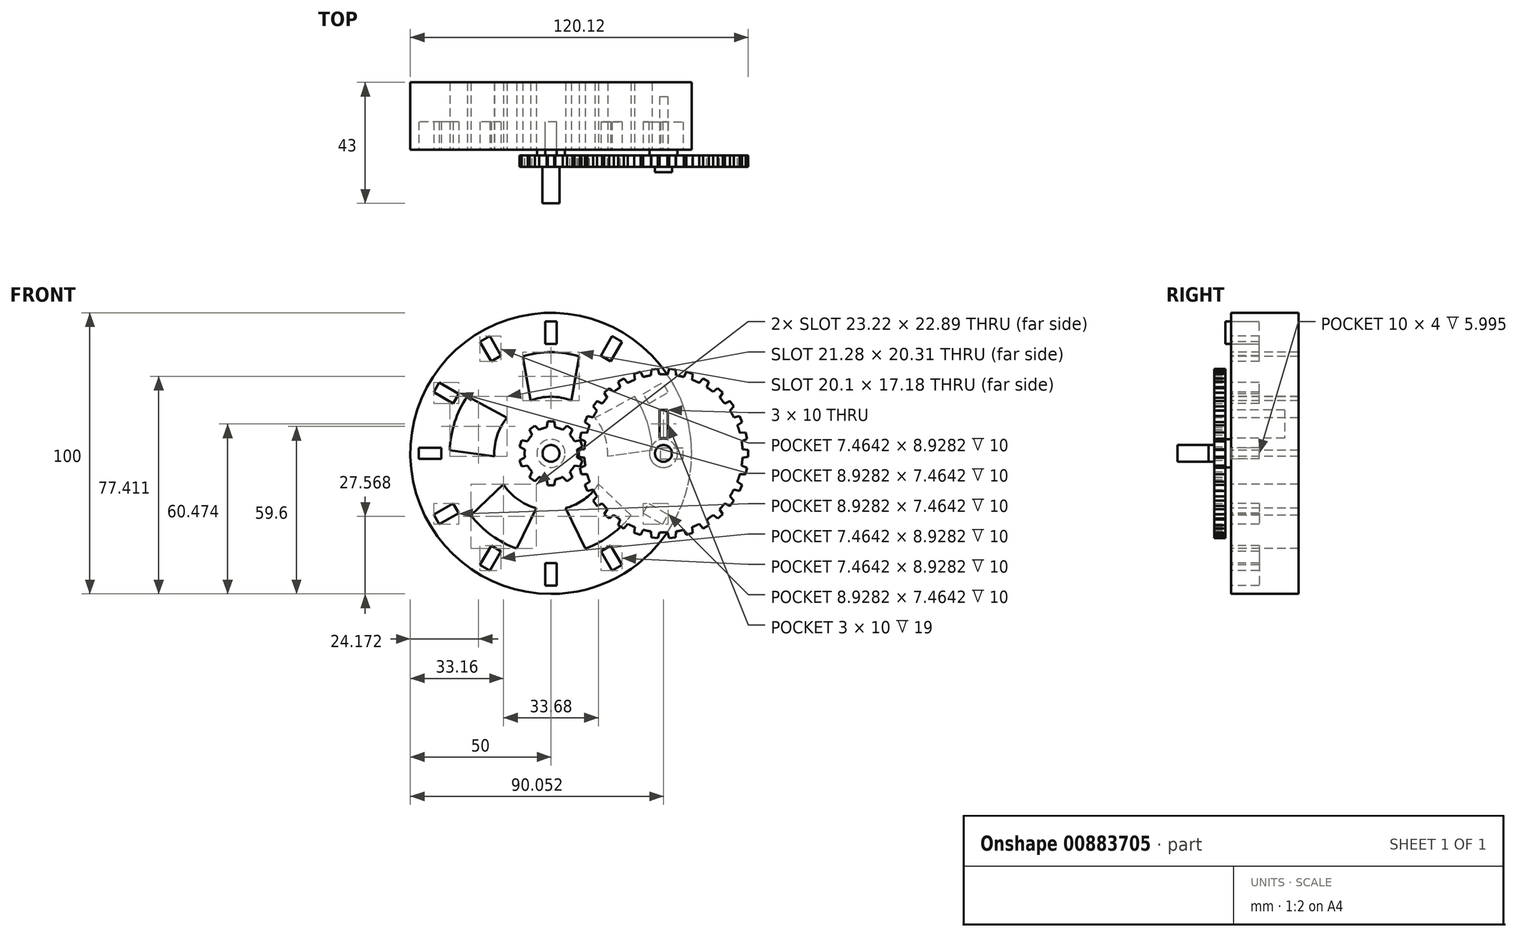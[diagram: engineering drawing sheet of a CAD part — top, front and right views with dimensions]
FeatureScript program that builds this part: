
annotation { "Feature Type Name" : "Feature", "Feature Type Description" : "" }
export const myFeature = defineFeature(function(context is Context, id is Id, definition is map)
    precondition{}
    {
        {
            assignVariable(context, id + "F0", {"name" : "DA", "anyValue" : 40});
        }
        {
            assignVariable(context, id + "F1", {"name" : "M", "anyValue" : 2.5});
        }
        {
            var Q0;
            Q0=qCreatedBy(makeId("Front.planeOp"),FACE);
            var sketch = newSketch(context, id + "F2", { "sketchPlane" : qUnion([Q0])});
            skCircle(sketch, "E0", {"center": v(0, 0) * mm, "radius": 50 * mm});
            skSolve(sketch);
        }
        {
            var Q0;
            Q0 = qSketchRegion(id + "F2", true);
            extrude(context, id + "F3", {"entities" : qUnion([Q0]), "depth" : 24 * mm, "offsetDistance" : 25 * mm});
        }
        {
            var Q0;
            Q0=makeQuery(id+"F3.opExtrude","CAP_FACE",FACE,{"disambiguationData":[OSD([sQuery(id+"F2.wireOp",EDGE,"E0")])],"isStart":false});
            var sketch = newSketch(context, id + "F4", { "sketchPlane" : qUnion([Q0])});
            skCircle(sketch, "E1", {"center": v(0, 0) * mm, "radius": 5 * mm});
            skCircle(sketch, "E2", {"center": v(40, 0) * mm, "radius": 5 * mm});
            skCircle(sketch, "E3", {"center": v(0, 0) * mm, "radius": 3 * mm});
            skCircle(sketch, "E4", {"center": v(40, 0) * mm, "radius": 3 * mm});
            skSolve(sketch);
        }
        {
            var Q0;
            Q0 = qSketchRegion(id + "F4", true);
            extrude(context, id + "F5", {"entities" : qUnion([Q0]), "operationType" : NewBodyOperationType.ADD, "depth" : 2 * mm, "offsetDistance" : 25 * mm});
        }
        {
            var Q0;
            Q0=makeQuery(id+"F5.boolean.opBoolean","SPLIT",FACE,{"disambiguationData":[TD([makeQuery(id+"F5.opExtrude","SWEPT_FACE",FACE,{"disambiguationData":[OSD([sQuery(id+"F4.wireOp",EDGE,"E3")])]})])],"derivedFrom":makeQuery(id+"F3.opExtrude","CAP_FACE",FACE,{"disambiguationData":[OSD([sQuery(id+"F2.wireOp",EDGE,"E0")])],"isStart":false})});
            extrude(context, id + "F6", {"entities" : qUnion([Q0]), "depth" : 19 * mm, "offsetDistance" : 25 * mm});
        }
        {
            var Q0;
            Q0=makeQuery(id+"F5.boolean.opBoolean","SPLIT",FACE,{"disambiguationData":[TD([makeQuery(id+"F5.opExtrude","SWEPT_FACE",FACE,{"disambiguationData":[OSD([sQuery(id+"F4.wireOp",EDGE,"E4")])]})])],"derivedFrom":makeQuery(id+"F3.opExtrude","CAP_FACE",FACE,{"disambiguationData":[OSD([sQuery(id+"F2.wireOp",EDGE,"E0")])],"isStart":false})});
            extrude(context, id + "F7", {"entities" : qUnion([Q0]), "depth" : 8 * mm, "offsetDistance" : 25 * mm});
        }
        {
            assignVariable(context, id + "F8", {"name" : "M", "anyValue" : 2.5});
        }
        {
            assignVariable(context, id + "F9", {"name" : "S", "anyValue" : 0.8});
        }
        {
            assignVariable(context, id + "F10", {"name" : "DL", "anyValue" : (getVariable(context, 'DA') - getVariable(context, 'M')) / 2});
        }
        {
            var Q0;
            Q0=makeQuery(id+"F5.opExtrude","CAP_FACE",FACE,{"disambiguationData":[OSD([sQuery(id+"F4.wireOp",EDGE,"E1"),sQuery(id+"F4.wireOp",EDGE,"E3")])],"isStart":false});
            var sketch = newSketch(context, id + "F11", { "sketchPlane" : qUnion([Q0])});
            skCircle(sketch, "E5", {"center": v(0, 0) * mm, "radius": 9.38 * mm});
            skLineSegment(sketch, "E6", {"start": v(1.55, 9.25) * mm, "end": v(1.18, 11.38) * mm});
            skLineSegment(sketch, "E7", {"start": v(1.18, 11.38) * mm, "end": v(0, 11.38) * mm});
            skLineSegment(sketch, "E8.MirrorCS", {"start": v(-1.18, 11.38) * mm, "end": v(0, 11.38) * mm});
            skLineSegment(sketch, "E9.MirrorCS", {"start": v(-1.55, 9.25) * mm, "end": v(-1.18, 11.38) * mm});
            skLineSegment(sketch, "E10.1.0", {"start": v(-5.73, 9.9) * mm, "end": v(-6.69, 9.2) * mm});
            skLineSegment(sketch, "E10.1.1", {"start": v(-7.64, 8.51) * mm, "end": v(-6.69, 9.2) * mm});
            skLineSegment(sketch, "E10.1.2", {"start": v(-6.7, 6.57) * mm, "end": v(-7.64, 8.51) * mm});
            skLineSegment(sketch, "E10.1.3", {"start": v(-4.18, 8.4) * mm, "end": v(-5.73, 9.9) * mm});
            skLineSegment(sketch, "E10.2.0", {"start": v(-10.45, 4.64) * mm, "end": v(-10.82, 3.52) * mm});
            skLineSegment(sketch, "E10.2.1", {"start": v(-11.18, 2.4) * mm, "end": v(-10.82, 3.52) * mm});
            skLineSegment(sketch, "E10.2.2", {"start": v(-9.27, 1.38) * mm, "end": v(-11.18, 2.4) * mm});
            skLineSegment(sketch, "E10.2.3", {"start": v(-8.31, 4.33) * mm, "end": v(-10.45, 4.64) * mm});
            skLineSegment(sketch, "E11.2.3.0", {"start": v(-11.18, -2.4) * mm, "end": v(-10.82, -3.52) * mm});
            skLineSegment(sketch, "E11.3.3.0", {"start": v(-10.45, -4.64) * mm, "end": v(-10.82, -3.52) * mm});
            skLineSegment(sketch, "E11.6.3.0", {"start": v(-8.31, -4.33) * mm, "end": v(-10.45, -4.64) * mm});
            skLineSegment(sketch, "E11.9.3.0", {"start": v(-9.27, -1.38) * mm, "end": v(-11.18, -2.4) * mm});
            skLineSegment(sketch, "E11.2.4.0", {"start": v(-7.64, -8.51) * mm, "end": v(-6.69, -9.2) * mm});
            skLineSegment(sketch, "E11.3.4.0", {"start": v(-5.73, -9.9) * mm, "end": v(-6.69, -9.2) * mm});
            skLineSegment(sketch, "E11.6.4.0", {"start": v(-4.18, -8.4) * mm, "end": v(-5.73, -9.9) * mm});
            skLineSegment(sketch, "E11.9.4.0", {"start": v(-6.7, -6.57) * mm, "end": v(-7.64, -8.51) * mm});
            skLineSegment(sketch, "E11.2.5.0", {"start": v(-1.18, -11.38) * mm, "end": v(0, -11.38) * mm});
            skLineSegment(sketch, "E11.3.5.0", {"start": v(1.18, -11.38) * mm, "end": v(0, -11.38) * mm});
            skLineSegment(sketch, "E11.6.5.0", {"start": v(1.55, -9.25) * mm, "end": v(1.18, -11.38) * mm});
            skLineSegment(sketch, "E11.9.5.0", {"start": v(-1.55, -9.25) * mm, "end": v(-1.18, -11.38) * mm});
            skLineSegment(sketch, "E11.2.6.0", {"start": v(5.73, -9.9) * mm, "end": v(6.69, -9.2) * mm});
            skLineSegment(sketch, "E11.3.6.0", {"start": v(7.64, -8.51) * mm, "end": v(6.69, -9.2) * mm});
            skLineSegment(sketch, "E11.6.6.0", {"start": v(6.7, -6.57) * mm, "end": v(7.64, -8.51) * mm});
            skLineSegment(sketch, "E11.9.6.0", {"start": v(4.18, -8.4) * mm, "end": v(5.73, -9.9) * mm});
            skLineSegment(sketch, "E11.2.7.0", {"start": v(10.45, -4.64) * mm, "end": v(10.82, -3.52) * mm});
            skLineSegment(sketch, "E11.3.7.0", {"start": v(11.18, -2.4) * mm, "end": v(10.82, -3.52) * mm});
            skLineSegment(sketch, "E11.6.7.0", {"start": v(9.27, -1.38) * mm, "end": v(11.18, -2.4) * mm});
            skLineSegment(sketch, "E11.9.7.0", {"start": v(8.31, -4.33) * mm, "end": v(10.45, -4.64) * mm});
            skLineSegment(sketch, "E11.2.8.0", {"start": v(11.18, 2.4) * mm, "end": v(10.82, 3.52) * mm});
            skLineSegment(sketch, "E11.3.8.0", {"start": v(10.45, 4.64) * mm, "end": v(10.82, 3.52) * mm});
            skLineSegment(sketch, "E11.6.8.0", {"start": v(8.31, 4.33) * mm, "end": v(10.45, 4.64) * mm});
            skLineSegment(sketch, "E11.9.8.0", {"start": v(9.27, 1.38) * mm, "end": v(11.18, 2.4) * mm});
            skLineSegment(sketch, "E11.2.9.0", {"start": v(7.64, 8.51) * mm, "end": v(6.69, 9.2) * mm});
            skLineSegment(sketch, "E11.3.9.0", {"start": v(5.73, 9.9) * mm, "end": v(6.69, 9.2) * mm});
            skLineSegment(sketch, "E11.6.9.0", {"start": v(4.18, 8.4) * mm, "end": v(5.73, 9.9) * mm});
            skLineSegment(sketch, "E11.9.9.0", {"start": v(6.7, 6.57) * mm, "end": v(7.64, 8.51) * mm});
            skSolve(sketch);
        }
        {
            var Q0;
            Q0 = qSketchRegion(id + "F11", true);
            extrude(context, id + "F12", {"entities" : qUnion([Q0]), "operationType" : NewBodyOperationType.ADD, "depth" : 4 * mm, "offsetDistance" : 25 * mm});
        }
        {
            var Q0;
            Q0=makeQuery(id+"F5.opExtrude","CAP_FACE",FACE,{"disambiguationData":[OSD([sQuery(id+"F4.wireOp",EDGE,"E2"),sQuery(id+"F4.wireOp",EDGE,"E4")])],"isStart":false});
            var sketch = newSketch(context, id + "F13", { "sketchPlane" : qUnion([Q0])});
            skCircle(sketch, "E12", {"center": v(40, 0) * mm, "radius": 28.12 * mm});
            skLineSegment(sketch, "E13", {"start": v(11.92, 1.54) * mm, "end": v(9.88, 1.18) * mm});
            skLineSegment(sketch, "E14", {"start": v(9.88, 1.18) * mm, "end": v(9.88, 0) * mm});
            skLineSegment(sketch, "E15.MirrorCS", {"start": v(9.88, -1.18) * mm, "end": v(9.88, 0) * mm});
            skLineSegment(sketch, "E16.MirrorCS", {"start": v(11.92, -1.54) * mm, "end": v(9.88, -1.18) * mm});
            skLineSegment(sketch, "E17.1.0", {"start": v(12.21, -4.33) * mm, "end": v(10.29, -5.11) * mm});
            skLineSegment(sketch, "E17.1.1", {"start": v(10.29, -5.11) * mm, "end": v(10.53, -6.26) * mm});
            skLineSegment(sketch, "E17.1.2", {"start": v(10.78, -7.42) * mm, "end": v(10.53, -6.26) * mm});
            skLineSegment(sketch, "E17.1.3", {"start": v(12.85, -7.34) * mm, "end": v(10.78, -7.42) * mm});
            skLineSegment(sketch, "E17.2.0", {"start": v(13.72, -10.02) * mm, "end": v(12, -11.18) * mm});
            skLineSegment(sketch, "E17.2.1", {"start": v(12, -11.18) * mm, "end": v(12.48, -12.25) * mm});
            skLineSegment(sketch, "E17.2.2", {"start": v(12.96, -13.33) * mm, "end": v(12.48, -12.25) * mm});
            skLineSegment(sketch, "E17.2.3", {"start": v(14.97, -12.83) * mm, "end": v(12.96, -13.33) * mm});
            skLineSegment(sketch, "E18.2.3.0", {"start": v(16.38, -15.26) * mm, "end": v(14.94, -16.75) * mm});
            skLineSegment(sketch, "E18.3.3.0", {"start": v(14.94, -16.75) * mm, "end": v(15.63, -17.7) * mm});
            skLineSegment(sketch, "E18.6.3.0", {"start": v(16.32, -18.66) * mm, "end": v(15.63, -17.7) * mm});
            skLineSegment(sketch, "E18.9.3.0", {"start": v(18.18, -17.75) * mm, "end": v(16.32, -18.66) * mm});
            skLineSegment(sketch, "E18.2.4.0", {"start": v(20.07, -19.84) * mm, "end": v(18.97, -21.6) * mm});
            skLineSegment(sketch, "E18.3.4.0", {"start": v(18.97, -21.6) * mm, "end": v(19.84, -22.39) * mm});
            skLineSegment(sketch, "E18.6.4.0", {"start": v(20.72, -23.18) * mm, "end": v(19.84, -22.39) * mm});
            skLineSegment(sketch, "E18.9.4.0", {"start": v(22.35, -21.9) * mm, "end": v(20.72, -23.18) * mm});
            skLineSegment(sketch, "E18.2.5.0", {"start": v(24.63, -23.55) * mm, "end": v(23.92, -25.5) * mm});
            skLineSegment(sketch, "E18.3.5.0", {"start": v(23.92, -25.5) * mm, "end": v(24.94, -26.09) * mm});
            skLineSegment(sketch, "E18.6.5.0", {"start": v(25.96, -26.68) * mm, "end": v(24.94, -26.09) * mm});
            skLineSegment(sketch, "E18.9.5.0", {"start": v(27.3, -25.09) * mm, "end": v(25.96, -26.68) * mm});
            skLineSegment(sketch, "E18.2.6.0", {"start": v(29.86, -26.23) * mm, "end": v(29.57, -28.29) * mm});
            skLineSegment(sketch, "E18.3.6.0", {"start": v(29.57, -28.29) * mm, "end": v(30.7, -28.65) * mm});
            skLineSegment(sketch, "E18.6.6.0", {"start": v(31.81, -29.01) * mm, "end": v(30.7, -28.65) * mm});
            skLineSegment(sketch, "E18.9.6.0", {"start": v(32.78, -27.18) * mm, "end": v(31.81, -29.01) * mm});
            skLineSegment(sketch, "E18.2.7.0", {"start": v(35.53, -27.77) * mm, "end": v(35.68, -29.84) * mm});
            skLineSegment(sketch, "E18.3.7.0", {"start": v(35.68, -29.84) * mm, "end": v(36.85, -29.96) * mm});
            skLineSegment(sketch, "E18.6.7.0", {"start": v(38.02, -30.08) * mm, "end": v(36.85, -29.96) * mm});
            skLineSegment(sketch, "E18.9.7.0", {"start": v(38.6, -28.09) * mm, "end": v(38.02, -30.08) * mm});
            skLineSegment(sketch, "E18.2.8.0", {"start": v(41.4, -28.09) * mm, "end": v(41.98, -30.08) * mm});
            skLineSegment(sketch, "E18.3.8.0", {"start": v(41.98, -30.08) * mm, "end": v(43.15, -29.96) * mm});
            skLineSegment(sketch, "E18.6.8.0", {"start": v(44.32, -29.84) * mm, "end": v(43.15, -29.96) * mm});
            skLineSegment(sketch, "E18.9.8.0", {"start": v(44.47, -27.77) * mm, "end": v(44.32, -29.84) * mm});
            skLineSegment(sketch, "E18.2.9.0", {"start": v(47.22, -27.18) * mm, "end": v(48.19, -29.01) * mm});
            skLineSegment(sketch, "E18.3.9.0", {"start": v(48.19, -29.01) * mm, "end": v(49.3, -28.65) * mm});
            skLineSegment(sketch, "E18.6.9.0", {"start": v(50.43, -28.29) * mm, "end": v(49.3, -28.65) * mm});
            skLineSegment(sketch, "E18.9.9.0", {"start": v(50.14, -26.23) * mm, "end": v(50.43, -28.29) * mm});
            skLineSegment(sketch, "E18.2.10.0", {"start": v(52.7, -25.09) * mm, "end": v(54.04, -26.68) * mm});
            skLineSegment(sketch, "E18.3.10.0", {"start": v(54.04, -26.68) * mm, "end": v(55.06, -26.09) * mm});
            skLineSegment(sketch, "E18.6.10.0", {"start": v(56.08, -25.5) * mm, "end": v(55.06, -26.09) * mm});
            skLineSegment(sketch, "E18.9.10.0", {"start": v(55.37, -23.55) * mm, "end": v(56.08, -25.5) * mm});
            skLineSegment(sketch, "E18.2.11.0", {"start": v(57.65, -21.9) * mm, "end": v(59.28, -23.18) * mm});
            skLineSegment(sketch, "E18.3.11.0", {"start": v(59.28, -23.18) * mm, "end": v(60.16, -22.39) * mm});
            skLineSegment(sketch, "E18.6.11.0", {"start": v(61.03, -21.6) * mm, "end": v(60.16, -22.39) * mm});
            skLineSegment(sketch, "E18.9.11.0", {"start": v(59.93, -19.84) * mm, "end": v(61.03, -21.6) * mm});
            skLineSegment(sketch, "E18.2.12.0", {"start": v(61.82, -17.75) * mm, "end": v(63.68, -18.66) * mm});
            skLineSegment(sketch, "E18.3.12.0", {"start": v(63.68, -18.66) * mm, "end": v(64.37, -17.7) * mm});
            skLineSegment(sketch, "E18.6.12.0", {"start": v(65.06, -16.75) * mm, "end": v(64.37, -17.7) * mm});
            skLineSegment(sketch, "E18.9.12.0", {"start": v(63.62, -15.26) * mm, "end": v(65.06, -16.75) * mm});
            skLineSegment(sketch, "E18.2.13.0", {"start": v(65.03, -12.83) * mm, "end": v(67.04, -13.33) * mm});
            skLineSegment(sketch, "E18.3.13.0", {"start": v(67.04, -13.33) * mm, "end": v(67.52, -12.25) * mm});
            skLineSegment(sketch, "E18.6.13.0", {"start": v(68, -11.18) * mm, "end": v(67.52, -12.25) * mm});
            skLineSegment(sketch, "E18.9.13.0", {"start": v(66.28, -10.02) * mm, "end": v(68, -11.18) * mm});
            skLineSegment(sketch, "E18.2.14.0", {"start": v(67.15, -7.34) * mm, "end": v(69.22, -7.42) * mm});
            skLineSegment(sketch, "E18.3.14.0", {"start": v(69.22, -7.42) * mm, "end": v(69.47, -6.26) * mm});
            skLineSegment(sketch, "E18.6.14.0", {"start": v(69.71, -5.11) * mm, "end": v(69.47, -6.26) * mm});
            skLineSegment(sketch, "E18.9.14.0", {"start": v(67.79, -4.33) * mm, "end": v(69.71, -5.11) * mm});
            skLineSegment(sketch, "E18.2.15.0", {"start": v(68.08, -1.54) * mm, "end": v(70.13, -1.18) * mm});
            skLineSegment(sketch, "E18.3.15.0", {"start": v(70.12, -1.18) * mm, "end": v(70.12, 0) * mm});
            skLineSegment(sketch, "E18.6.15.0", {"start": v(70.12, 1.18) * mm, "end": v(70.12, 0) * mm});
            skLineSegment(sketch, "E18.9.15.0", {"start": v(68.08, 1.54) * mm, "end": v(70.13, 1.18) * mm});
            skLineSegment(sketch, "E18.2.16.0", {"start": v(67.79, 4.33) * mm, "end": v(69.71, 5.11) * mm});
            skLineSegment(sketch, "E18.3.16.0", {"start": v(69.71, 5.11) * mm, "end": v(69.47, 6.26) * mm});
            skLineSegment(sketch, "E18.6.16.0", {"start": v(69.22, 7.42) * mm, "end": v(69.47, 6.26) * mm});
            skLineSegment(sketch, "E18.9.16.0", {"start": v(67.15, 7.34) * mm, "end": v(69.22, 7.42) * mm});
            skLineSegment(sketch, "E18.2.17.0", {"start": v(66.28, 10.02) * mm, "end": v(68, 11.18) * mm});
            skLineSegment(sketch, "E18.3.17.0", {"start": v(68, 11.18) * mm, "end": v(67.52, 12.25) * mm});
            skLineSegment(sketch, "E18.6.17.0", {"start": v(67.04, 13.33) * mm, "end": v(67.52, 12.25) * mm});
            skLineSegment(sketch, "E18.9.17.0", {"start": v(65.03, 12.83) * mm, "end": v(67.04, 13.33) * mm});
            skLineSegment(sketch, "E18.2.18.0", {"start": v(63.62, 15.26) * mm, "end": v(65.06, 16.75) * mm});
            skLineSegment(sketch, "E18.3.18.0", {"start": v(65.06, 16.75) * mm, "end": v(64.37, 17.7) * mm});
            skLineSegment(sketch, "E18.6.18.0", {"start": v(63.68, 18.66) * mm, "end": v(64.37, 17.7) * mm});
            skLineSegment(sketch, "E18.9.18.0", {"start": v(61.82, 17.75) * mm, "end": v(63.68, 18.66) * mm});
            skLineSegment(sketch, "E18.2.19.0", {"start": v(59.93, 19.84) * mm, "end": v(61.03, 21.6) * mm});
            skLineSegment(sketch, "E18.3.19.0", {"start": v(61.03, 21.6) * mm, "end": v(60.16, 22.39) * mm});
            skLineSegment(sketch, "E18.6.19.0", {"start": v(59.28, 23.18) * mm, "end": v(60.16, 22.39) * mm});
            skLineSegment(sketch, "E18.9.19.0", {"start": v(57.65, 21.9) * mm, "end": v(59.28, 23.18) * mm});
            skLineSegment(sketch, "E18.2.20.0", {"start": v(55.37, 23.55) * mm, "end": v(56.08, 25.5) * mm});
            skLineSegment(sketch, "E18.3.20.0", {"start": v(56.08, 25.5) * mm, "end": v(55.06, 26.09) * mm});
            skLineSegment(sketch, "E18.6.20.0", {"start": v(54.04, 26.68) * mm, "end": v(55.06, 26.09) * mm});
            skLineSegment(sketch, "E18.9.20.0", {"start": v(52.7, 25.09) * mm, "end": v(54.04, 26.68) * mm});
            skLineSegment(sketch, "E18.2.21.0", {"start": v(50.14, 26.23) * mm, "end": v(50.43, 28.29) * mm});
            skLineSegment(sketch, "E18.3.21.0", {"start": v(50.43, 28.29) * mm, "end": v(49.3, 28.65) * mm});
            skLineSegment(sketch, "E18.6.21.0", {"start": v(48.19, 29.01) * mm, "end": v(49.3, 28.65) * mm});
            skLineSegment(sketch, "E18.9.21.0", {"start": v(47.22, 27.18) * mm, "end": v(48.19, 29.01) * mm});
            skLineSegment(sketch, "E18.2.22.0", {"start": v(44.47, 27.77) * mm, "end": v(44.32, 29.84) * mm});
            skLineSegment(sketch, "E18.3.22.0", {"start": v(44.32, 29.84) * mm, "end": v(43.15, 29.96) * mm});
            skLineSegment(sketch, "E18.6.22.0", {"start": v(41.98, 30.08) * mm, "end": v(43.15, 29.96) * mm});
            skLineSegment(sketch, "E18.9.22.0", {"start": v(41.4, 28.09) * mm, "end": v(41.98, 30.08) * mm});
            skLineSegment(sketch, "E18.2.23.0", {"start": v(38.6, 28.09) * mm, "end": v(38.02, 30.08) * mm});
            skLineSegment(sketch, "E18.3.23.0", {"start": v(38.02, 30.08) * mm, "end": v(36.85, 29.96) * mm});
            skLineSegment(sketch, "E18.6.23.0", {"start": v(35.68, 29.84) * mm, "end": v(36.85, 29.96) * mm});
            skLineSegment(sketch, "E18.9.23.0", {"start": v(35.53, 27.77) * mm, "end": v(35.68, 29.84) * mm});
            skLineSegment(sketch, "E18.2.24.0", {"start": v(32.78, 27.18) * mm, "end": v(31.81, 29.01) * mm});
            skLineSegment(sketch, "E18.3.24.0", {"start": v(31.81, 29.01) * mm, "end": v(30.7, 28.65) * mm});
            skLineSegment(sketch, "E18.6.24.0", {"start": v(29.57, 28.29) * mm, "end": v(30.7, 28.65) * mm});
            skLineSegment(sketch, "E18.9.24.0", {"start": v(29.86, 26.23) * mm, "end": v(29.57, 28.29) * mm});
            skLineSegment(sketch, "E18.2.25.0", {"start": v(27.3, 25.09) * mm, "end": v(25.96, 26.68) * mm});
            skLineSegment(sketch, "E18.3.25.0", {"start": v(25.96, 26.68) * mm, "end": v(24.94, 26.09) * mm});
            skLineSegment(sketch, "E18.6.25.0", {"start": v(23.92, 25.5) * mm, "end": v(24.94, 26.09) * mm});
            skLineSegment(sketch, "E18.9.25.0", {"start": v(24.63, 23.55) * mm, "end": v(23.92, 25.5) * mm});
            skLineSegment(sketch, "E18.2.26.0", {"start": v(22.35, 21.9) * mm, "end": v(20.72, 23.18) * mm});
            skLineSegment(sketch, "E18.3.26.0", {"start": v(20.72, 23.18) * mm, "end": v(19.84, 22.39) * mm});
            skLineSegment(sketch, "E18.6.26.0", {"start": v(18.97, 21.6) * mm, "end": v(19.84, 22.39) * mm});
            skLineSegment(sketch, "E18.9.26.0", {"start": v(20.07, 19.84) * mm, "end": v(18.97, 21.6) * mm});
            skLineSegment(sketch, "E18.2.27.0", {"start": v(18.18, 17.75) * mm, "end": v(16.32, 18.66) * mm});
            skLineSegment(sketch, "E18.3.27.0", {"start": v(16.32, 18.66) * mm, "end": v(15.63, 17.7) * mm});
            skLineSegment(sketch, "E18.6.27.0", {"start": v(14.94, 16.75) * mm, "end": v(15.63, 17.7) * mm});
            skLineSegment(sketch, "E18.9.27.0", {"start": v(16.38, 15.26) * mm, "end": v(14.94, 16.75) * mm});
            skLineSegment(sketch, "E18.2.28.0", {"start": v(14.97, 12.83) * mm, "end": v(12.96, 13.33) * mm});
            skLineSegment(sketch, "E18.3.28.0", {"start": v(12.96, 13.33) * mm, "end": v(12.48, 12.25) * mm});
            skLineSegment(sketch, "E18.6.28.0", {"start": v(12, 11.18) * mm, "end": v(12.48, 12.25) * mm});
            skLineSegment(sketch, "E18.9.28.0", {"start": v(13.72, 10.02) * mm, "end": v(12, 11.18) * mm});
            skLineSegment(sketch, "E18.2.29.0", {"start": v(12.85, 7.34) * mm, "end": v(10.78, 7.42) * mm});
            skLineSegment(sketch, "E18.3.29.0", {"start": v(10.78, 7.42) * mm, "end": v(10.53, 6.26) * mm});
            skLineSegment(sketch, "E18.6.29.0", {"start": v(10.29, 5.11) * mm, "end": v(10.53, 6.26) * mm});
            skLineSegment(sketch, "E18.9.29.0", {"start": v(12.21, 4.33) * mm, "end": v(10.29, 5.11) * mm});
            skSolve(sketch);
        }
        {
            var Q0;
            Q0 = qSketchRegion(id + "F13", true);
            extrude(context, id + "F14", {"entities" : qUnion([Q0]), "operationType" : NewBodyOperationType.ADD, "depth" : 4 * mm, "offsetDistance" : 25 * mm});
        }
        {
            var Q0;
            {var subQ0=sQuery(id+"F2.wireOp",EDGE,"E0");Q0=makeQuery(id+"F5.boolean.opBoolean","SPLIT",FACE,{"disambiguationData":[TD([makeQuery(id+"F3.opExtrude","SWEPT_FACE",FACE,{"disambiguationData":[OSD([subQ0])]})])],"derivedFrom":makeQuery(id+"F3.opExtrude","CAP_FACE",FACE,{"disambiguationData":[OSD([subQ0])],"isStart":false})});}
            var sketch = newSketch(context, id + "F15", { "sketchPlane" : qUnion([Q0])});
            skLineSegment(sketch, "E19.bottom", {"start": v(2, 39) * mm, "end": v(-2, 39) * mm});
            skLineSegment(sketch, "E19.top", {"start": v(2, 47) * mm, "end": v(-2, 47) * mm});
            skLineSegment(sketch, "E19.left", {"start": v(2, 39) * mm, "end": v(2, 47) * mm});
            skLineSegment(sketch, "E19.right", {"start": v(-2, 39) * mm, "end": v(-2, 47) * mm});
            skPoint(sketch, "E19.middle", {"position": v(0, 43) * mm});
            skLineSegment(sketch, "E20.1.0", {"start": v(-21.77, 41.7) * mm, "end": v(-25.23, 39.7) * mm});
            skLineSegment(sketch, "E20.1.1", {"start": v(-17.77, 34.77) * mm, "end": v(-21.77, 41.7) * mm});
            skLineSegment(sketch, "E20.1.2", {"start": v(-17.77, 34.77) * mm, "end": v(-21.23, 32.77) * mm});
            skLineSegment(sketch, "E20.1.3", {"start": v(-21.23, 32.77) * mm, "end": v(-25.23, 39.7) * mm});
            skLineSegment(sketch, "E20.2.0", {"start": v(-39.7, 25.23) * mm, "end": v(-41.7, 21.77) * mm});
            skLineSegment(sketch, "E20.2.1", {"start": v(-32.77, 21.23) * mm, "end": v(-39.7, 25.23) * mm});
            skLineSegment(sketch, "E20.2.2", {"start": v(-32.77, 21.23) * mm, "end": v(-34.77, 17.77) * mm});
            skLineSegment(sketch, "E20.2.3", {"start": v(-34.77, 17.77) * mm, "end": v(-41.7, 21.77) * mm});
            skPoint(sketch, "E20.center", {"position": v(0, 0) * mm});
            skLineSegment(sketch, "E21.2.3.0", {"start": v(-47, 2) * mm, "end": v(-47, -2) * mm});
            skLineSegment(sketch, "E21.3.3.0", {"start": v(-39, 2) * mm, "end": v(-47, 2) * mm});
            skLineSegment(sketch, "E21.6.3.0", {"start": v(-39, 2) * mm, "end": v(-39, -2) * mm});
            skLineSegment(sketch, "E21.9.3.0", {"start": v(-39, -2) * mm, "end": v(-47, -2) * mm});
            skLineSegment(sketch, "E21.2.4.0", {"start": v(-41.7, -21.77) * mm, "end": v(-39.7, -25.23) * mm});
            skLineSegment(sketch, "E21.3.4.0", {"start": v(-34.77, -17.77) * mm, "end": v(-41.7, -21.77) * mm});
            skLineSegment(sketch, "E21.6.4.0", {"start": v(-34.77, -17.77) * mm, "end": v(-32.77, -21.23) * mm});
            skLineSegment(sketch, "E21.9.4.0", {"start": v(-32.77, -21.23) * mm, "end": v(-39.7, -25.23) * mm});
            skLineSegment(sketch, "E21.2.5.0", {"start": v(-25.23, -39.7) * mm, "end": v(-21.77, -41.7) * mm});
            skLineSegment(sketch, "E21.3.5.0", {"start": v(-21.23, -32.77) * mm, "end": v(-25.23, -39.7) * mm});
            skLineSegment(sketch, "E21.6.5.0", {"start": v(-21.23, -32.77) * mm, "end": v(-17.77, -34.77) * mm});
            skLineSegment(sketch, "E21.9.5.0", {"start": v(-17.77, -34.77) * mm, "end": v(-21.77, -41.7) * mm});
            skLineSegment(sketch, "E21.2.6.0", {"start": v(-2, -47) * mm, "end": v(2, -47) * mm});
            skLineSegment(sketch, "E21.3.6.0", {"start": v(-2, -39) * mm, "end": v(-2, -47) * mm});
            skLineSegment(sketch, "E21.6.6.0", {"start": v(-2, -39) * mm, "end": v(2, -39) * mm});
            skLineSegment(sketch, "E21.9.6.0", {"start": v(2, -39) * mm, "end": v(2, -47) * mm});
            skLineSegment(sketch, "E21.2.7.0", {"start": v(21.77, -41.7) * mm, "end": v(25.23, -39.7) * mm});
            skLineSegment(sketch, "E21.3.7.0", {"start": v(17.77, -34.77) * mm, "end": v(21.77, -41.7) * mm});
            skLineSegment(sketch, "E21.6.7.0", {"start": v(17.77, -34.77) * mm, "end": v(21.23, -32.77) * mm});
            skLineSegment(sketch, "E21.9.7.0", {"start": v(21.23, -32.77) * mm, "end": v(25.23, -39.7) * mm});
            skLineSegment(sketch, "E21.2.8.0", {"start": v(39.7, -25.23) * mm, "end": v(41.7, -21.77) * mm});
            skLineSegment(sketch, "E21.3.8.0", {"start": v(32.77, -21.23) * mm, "end": v(39.7, -25.23) * mm});
            skLineSegment(sketch, "E21.6.8.0", {"start": v(32.77, -21.23) * mm, "end": v(34.77, -17.77) * mm});
            skLineSegment(sketch, "E21.9.8.0", {"start": v(34.77, -17.77) * mm, "end": v(41.7, -21.77) * mm});
            skLineSegment(sketch, "E21.2.9.0", {"start": v(47, -2) * mm, "end": v(47, 2) * mm});
            skLineSegment(sketch, "E21.3.9.0", {"start": v(39, -2) * mm, "end": v(47, -2) * mm});
            skLineSegment(sketch, "E21.6.9.0", {"start": v(39, -2) * mm, "end": v(39, 2) * mm});
            skLineSegment(sketch, "E21.9.9.0", {"start": v(39, 2) * mm, "end": v(47, 2) * mm});
            skLineSegment(sketch, "E21.2.10.0", {"start": v(41.7, 21.77) * mm, "end": v(39.7, 25.23) * mm});
            skLineSegment(sketch, "E21.3.10.0", {"start": v(34.77, 17.77) * mm, "end": v(41.7, 21.77) * mm});
            skLineSegment(sketch, "E21.6.10.0", {"start": v(34.77, 17.77) * mm, "end": v(32.77, 21.23) * mm});
            skLineSegment(sketch, "E21.9.10.0", {"start": v(32.77, 21.23) * mm, "end": v(39.7, 25.23) * mm});
            skLineSegment(sketch, "E21.2.11.0", {"start": v(25.23, 39.7) * mm, "end": v(21.77, 41.7) * mm});
            skLineSegment(sketch, "E21.3.11.0", {"start": v(21.23, 32.77) * mm, "end": v(25.23, 39.7) * mm});
            skLineSegment(sketch, "E21.6.11.0", {"start": v(21.23, 32.77) * mm, "end": v(17.77, 34.77) * mm});
            skLineSegment(sketch, "E21.9.11.0", {"start": v(17.77, 34.77) * mm, "end": v(21.77, 41.7) * mm});
            skSolve(sketch);
        }
        {
            var Q0;
            Q0 = qSketchRegion(id + "F15", true);
            extrude(context, id + "F16", {"entities" : qUnion([Q0]), "operationType" : NewBodyOperationType.REMOVE, "oppositeDirection" : true, "depth" : 10 * mm, "offsetDistance" : 25 * mm});
        }
        {
            var Q0;
            Q0=makeQuery(id+"F16.boolean.opBoolean","COPY",FACE,{"derivedFrom":makeQuery(id+"F16.opExtrude","CAP_FACE",FACE,{"disambiguationData":[OSD([sQuery(id+"F15.wireOp",EDGE,"E19.bottom"),sQuery(id+"F15.wireOp",EDGE,"E19.top"),sQuery(id+"F15.wireOp",EDGE,"E19.left"),sQuery(id+"F15.wireOp",EDGE,"E19.right")])],"isStart":false})});
            extrude(context, id + "F17", {"entities" : qUnion([Q0]), "depth" : 12 * mm, "offsetDistance" : 25 * mm});
        }
        {
            var Q0;
            {var subQ0=sQuery(id+"F2.wireOp",EDGE,"E0");Q0=makeQuery(id+"F5.boolean.opBoolean","SPLIT",FACE,{"disambiguationData":[TD([makeQuery(id+"F3.opExtrude","SWEPT_FACE",FACE,{"disambiguationData":[OSD([subQ0])]})])],"derivedFrom":makeQuery(id+"F3.opExtrude","CAP_FACE",FACE,{"disambiguationData":[OSD([subQ0])],"isStart":false})});}
            var sketch = newSketch(context, id + "F18", { "sketchPlane" : qUnion([Q0])});
            skArc(sketch, "E22", {"start": v(-7.21, 18.82) * mm, "mid": v(-3.67, 19.82) * mm, "end": v(0, 20.16) * mm});
            skArc(sketch, "E23", {"start": v(-10.05, 34.57) * mm, "mid": v(-5.08, 35.64) * mm, "end": v(0, 36) * mm});
            skLineSegment(sketch, "E24", {"start": v(-10.05, 34.57) * mm, "end": v(-7.21, 18.82) * mm});
            skArc(sketch, "E25.MirrorCS", {"start": v(10.05, 34.57) * mm, "mid": v(5.08, 35.64) * mm, "end": v(0, 36) * mm});
            skLineSegment(sketch, "E26.MirrorCS", {"start": v(10.05, 34.57) * mm, "end": v(7.21, 18.82) * mm});
            skArc(sketch, "E27.MirrorCS", {"start": v(7.21, 18.82) * mm, "mid": v(3.67, 19.82) * mm, "end": v(0, 20.16) * mm});
            skArc(sketch, "E28.1.0", {"start": v(-35.98, 1.12) * mm, "mid": v(-35.46, 6.18) * mm, "end": v(-34.24, 11.12) * mm});
            skArc(sketch, "E28.1.1", {"start": v(-29.77, 20.24) * mm, "mid": v(-32.33, 15.84) * mm, "end": v(-34.24, 11.12) * mm});
            skLineSegment(sketch, "E28.1.2", {"start": v(-29.77, 20.24) * mm, "end": v(-15.67, 12.68) * mm});
            skArc(sketch, "E28.1.3", {"start": v(-15.67, 12.68) * mm, "mid": v(-17.72, 9.61) * mm, "end": v(-19.17, 6.23) * mm});
            skArc(sketch, "E28.1.4", {"start": v(-20.13, -1.04) * mm, "mid": v(-19.98, 2.64) * mm, "end": v(-19.17, 6.23) * mm});
            skLineSegment(sketch, "E28.1.5", {"start": v(-35.98, 1.12) * mm, "end": v(-20.13, -1.04) * mm});
            skArc(sketch, "E28.2.0", {"start": v(-12.19, -33.87) * mm, "mid": v(-16.84, -31.82) * mm, "end": v(-21.16, -29.12) * mm});
            skArc(sketch, "E28.2.1", {"start": v(-28.45, -22.06) * mm, "mid": v(-25.06, -25.85) * mm, "end": v(-21.16, -29.12) * mm});
            skLineSegment(sketch, "E28.2.2", {"start": v(-28.45, -22.06) * mm, "end": v(-16.9, -10.99) * mm});
            skArc(sketch, "E28.2.3", {"start": v(-16.9, -10.99) * mm, "mid": v(-14.62, -13.88) * mm, "end": v(-11.85, -16.3) * mm});
            skArc(sketch, "E28.2.4", {"start": v(-5.23, -19.47) * mm, "mid": v(-8.68, -18.2) * mm, "end": v(-11.85, -16.3) * mm});
            skLineSegment(sketch, "E28.2.5", {"start": v(-12.19, -33.87) * mm, "end": v(-5.23, -19.47) * mm});
            skArc(sketch, "E29.2.3.0", {"start": v(28.45, -22.06) * mm, "mid": v(25.06, -25.85) * mm, "end": v(21.16, -29.12) * mm});
            skArc(sketch, "E29.4.3.0", {"start": v(12.19, -33.87) * mm, "mid": v(16.84, -31.82) * mm, "end": v(21.16, -29.12) * mm});
            skLineSegment(sketch, "E29.8.3.0", {"start": v(12.19, -33.87) * mm, "end": v(5.23, -19.47) * mm});
            skArc(sketch, "E29.11.3.0", {"start": v(5.23, -19.47) * mm, "mid": v(8.68, -18.2) * mm, "end": v(11.85, -16.3) * mm});
            skArc(sketch, "E29.15.3.0", {"start": v(16.9, -10.99) * mm, "mid": v(14.62, -13.88) * mm, "end": v(11.85, -16.3) * mm});
            skLineSegment(sketch, "E29.19.3.0", {"start": v(28.45, -22.06) * mm, "end": v(16.9, -10.99) * mm});
            skArc(sketch, "E29.2.4.0", {"start": v(29.77, 20.24) * mm, "mid": v(32.33, 15.84) * mm, "end": v(34.24, 11.12) * mm});
            skArc(sketch, "E29.4.4.0", {"start": v(35.98, 1.12) * mm, "mid": v(35.46, 6.18) * mm, "end": v(34.24, 11.12) * mm});
            skLineSegment(sketch, "E29.8.4.0", {"start": v(35.98, 1.12) * mm, "end": v(20.13, -1.04) * mm});
            skArc(sketch, "E29.11.4.0", {"start": v(20.13, -1.04) * mm, "mid": v(19.98, 2.64) * mm, "end": v(19.17, 6.23) * mm});
            skArc(sketch, "E29.15.4.0", {"start": v(15.67, 12.68) * mm, "mid": v(17.72, 9.61) * mm, "end": v(19.17, 6.23) * mm});
            skLineSegment(sketch, "E29.19.4.0", {"start": v(29.77, 20.24) * mm, "end": v(15.67, 12.68) * mm});
            skSolve(sketch);
        }
        {
            var Q0;
            Q0 = qSketchRegion(id + "F18", true);
            extrude(context, id + "F19", {"entities" : qUnion([Q0]), "operationType" : NewBodyOperationType.REMOVE, "oppositeDirection" : true, "depth" : 25 * mm, "offsetDistance" : 25 * mm});
        }
        {
            var Q0;
            Q0=makeQuery(id+"F14.opExtrude","CAP_FACE",FACE,{"disambiguationData":[OSD([sQuery(id+"F13.wireOp",EDGE,"E12"),sQuery(id+"F13.wireOp",EDGE,"E13"),sQuery(id+"F13.wireOp",EDGE,"E14"),sQuery(id+"F13.wireOp",EDGE,"E15.MirrorCS"),sQuery(id+"F13.wireOp",EDGE,"E16.MirrorCS"),sQuery(id+"F13.wireOp",EDGE,"E17.1.0"),sQuery(id+"F13.wireOp",EDGE,"E17.1.1"),sQuery(id+"F13.wireOp",EDGE,"E17.1.2"),sQuery(id+"F13.wireOp",EDGE,"E17.1.3"),sQuery(id+"F13.wireOp",EDGE,"E17.2.0"),sQuery(id+"F13.wireOp",EDGE,"E17.2.1"),sQuery(id+"F13.wireOp",EDGE,"E17.2.2"),sQuery(id+"F13.wireOp",EDGE,"E17.2.3"),sQuery(id+"F13.wireOp",EDGE,"E18.2.3.0"),sQuery(id+"F13.wireOp",EDGE,"E18.3.3.0"),sQuery(id+"F13.wireOp",EDGE,"E18.6.3.0"),sQuery(id+"F13.wireOp",EDGE,"E18.9.3.0"),sQuery(id+"F13.wireOp",EDGE,"E18.2.4.0"),sQuery(id+"F13.wireOp",EDGE,"E18.3.4.0"),sQuery(id+"F13.wireOp",EDGE,"E18.6.4.0"),sQuery(id+"F13.wireOp",EDGE,"E18.9.4.0"),sQuery(id+"F13.wireOp",EDGE,"E18.2.5.0"),sQuery(id+"F13.wireOp",EDGE,"E18.3.5.0"),sQuery(id+"F13.wireOp",EDGE,"E18.6.5.0"),sQuery(id+"F13.wireOp",EDGE,"E18.9.5.0"),sQuery(id+"F13.wireOp",EDGE,"E18.2.6.0"),sQuery(id+"F13.wireOp",EDGE,"E18.3.6.0"),sQuery(id+"F13.wireOp",EDGE,"E18.6.6.0"),sQuery(id+"F13.wireOp",EDGE,"E18.9.6.0"),sQuery(id+"F13.wireOp",EDGE,"E18.2.7.0"),sQuery(id+"F13.wireOp",EDGE,"E18.3.7.0"),sQuery(id+"F13.wireOp",EDGE,"E18.6.7.0"),sQuery(id+"F13.wireOp",EDGE,"E18.9.7.0"),sQuery(id+"F13.wireOp",EDGE,"E18.2.8.0"),sQuery(id+"F13.wireOp",EDGE,"E18.3.8.0"),sQuery(id+"F13.wireOp",EDGE,"E18.6.8.0"),sQuery(id+"F13.wireOp",EDGE,"E18.9.8.0"),sQuery(id+"F13.wireOp",EDGE,"E18.2.9.0"),sQuery(id+"F13.wireOp",EDGE,"E18.3.9.0"),sQuery(id+"F13.wireOp",EDGE,"E18.6.9.0"),sQuery(id+"F13.wireOp",EDGE,"E18.9.9.0"),sQuery(id+"F13.wireOp",EDGE,"E18.2.10.0"),sQuery(id+"F13.wireOp",EDGE,"E18.3.10.0"),sQuery(id+"F13.wireOp",EDGE,"E18.6.10.0"),sQuery(id+"F13.wireOp",EDGE,"E18.9.10.0"),sQuery(id+"F13.wireOp",EDGE,"E18.2.11.0"),sQuery(id+"F13.wireOp",EDGE,"E18.3.11.0"),sQuery(id+"F13.wireOp",EDGE,"E18.6.11.0"),sQuery(id+"F13.wireOp",EDGE,"E18.9.11.0"),sQuery(id+"F13.wireOp",EDGE,"E18.2.12.0"),sQuery(id+"F13.wireOp",EDGE,"E18.3.12.0"),sQuery(id+"F13.wireOp",EDGE,"E18.6.12.0"),sQuery(id+"F13.wireOp",EDGE,"E18.9.12.0"),sQuery(id+"F13.wireOp",EDGE,"E18.2.13.0"),sQuery(id+"F13.wireOp",EDGE,"E18.3.13.0"),sQuery(id+"F13.wireOp",EDGE,"E18.6.13.0"),sQuery(id+"F13.wireOp",EDGE,"E18.9.13.0"),sQuery(id+"F13.wireOp",EDGE,"E18.2.14.0"),sQuery(id+"F13.wireOp",EDGE,"E18.3.14.0"),sQuery(id+"F13.wireOp",EDGE,"E18.6.14.0"),sQuery(id+"F13.wireOp",EDGE,"E18.9.14.0"),sQuery(id+"F13.wireOp",EDGE,"E18.2.15.0"),sQuery(id+"F13.wireOp",EDGE,"E18.3.15.0"),sQuery(id+"F13.wireOp",EDGE,"E18.6.15.0"),sQuery(id+"F13.wireOp",EDGE,"E18.9.15.0"),sQuery(id+"F13.wireOp",EDGE,"E18.2.16.0"),sQuery(id+"F13.wireOp",EDGE,"E18.3.16.0"),sQuery(id+"F13.wireOp",EDGE,"E18.6.16.0"),sQuery(id+"F13.wireOp",EDGE,"E18.9.16.0"),sQuery(id+"F13.wireOp",EDGE,"E18.2.17.0"),sQuery(id+"F13.wireOp",EDGE,"E18.3.17.0"),sQuery(id+"F13.wireOp",EDGE,"E18.6.17.0"),sQuery(id+"F13.wireOp",EDGE,"E18.9.17.0"),sQuery(id+"F13.wireOp",EDGE,"E18.2.18.0"),sQuery(id+"F13.wireOp",EDGE,"E18.3.18.0"),sQuery(id+"F13.wireOp",EDGE,"E18.6.18.0"),sQuery(id+"F13.wireOp",EDGE,"E18.9.18.0"),sQuery(id+"F13.wireOp",EDGE,"E18.2.19.0"),sQuery(id+"F13.wireOp",EDGE,"E18.3.19.0"),sQuery(id+"F13.wireOp",EDGE,"E18.6.19.0"),sQuery(id+"F13.wireOp",EDGE,"E18.9.19.0"),sQuery(id+"F13.wireOp",EDGE,"E18.2.20.0"),sQuery(id+"F13.wireOp",EDGE,"E18.3.20.0"),sQuery(id+"F13.wireOp",EDGE,"E18.6.20.0"),sQuery(id+"F13.wireOp",EDGE,"E18.9.20.0"),sQuery(id+"F13.wireOp",EDGE,"E18.2.21.0"),sQuery(id+"F13.wireOp",EDGE,"E18.3.21.0"),sQuery(id+"F13.wireOp",EDGE,"E18.6.21.0"),sQuery(id+"F13.wireOp",EDGE,"E18.9.21.0"),sQuery(id+"F13.wireOp",EDGE,"E18.2.22.0"),sQuery(id+"F13.wireOp",EDGE,"E18.3.22.0"),sQuery(id+"F13.wireOp",EDGE,"E18.6.22.0"),sQuery(id+"F13.wireOp",EDGE,"E18.9.22.0"),sQuery(id+"F13.wireOp",EDGE,"E18.2.23.0"),sQuery(id+"F13.wireOp",EDGE,"E18.3.23.0"),sQuery(id+"F13.wireOp",EDGE,"E18.6.23.0"),sQuery(id+"F13.wireOp",EDGE,"E18.9.23.0"),sQuery(id+"F13.wireOp",EDGE,"E18.2.24.0"),sQuery(id+"F13.wireOp",EDGE,"E18.3.24.0"),sQuery(id+"F13.wireOp",EDGE,"E18.6.24.0"),sQuery(id+"F13.wireOp",EDGE,"E18.9.24.0"),sQuery(id+"F13.wireOp",EDGE,"E18.2.25.0"),sQuery(id+"F13.wireOp",EDGE,"E18.3.25.0"),sQuery(id+"F13.wireOp",EDGE,"E18.6.25.0"),sQuery(id+"F13.wireOp",EDGE,"E18.9.25.0"),sQuery(id+"F13.wireOp",EDGE,"E18.2.26.0"),sQuery(id+"F13.wireOp",EDGE,"E18.3.26.0"),sQuery(id+"F13.wireOp",EDGE,"E18.6.26.0"),sQuery(id+"F13.wireOp",EDGE,"E18.9.26.0"),sQuery(id+"F13.wireOp",EDGE,"E18.2.27.0"),sQuery(id+"F13.wireOp",EDGE,"E18.3.27.0"),sQuery(id+"F13.wireOp",EDGE,"E18.6.27.0"),sQuery(id+"F13.wireOp",EDGE,"E18.9.27.0"),sQuery(id+"F13.wireOp",EDGE,"E18.2.28.0"),sQuery(id+"F13.wireOp",EDGE,"E18.3.28.0"),sQuery(id+"F13.wireOp",EDGE,"E18.6.28.0"),sQuery(id+"F13.wireOp",EDGE,"E18.9.28.0"),sQuery(id+"F13.wireOp",EDGE,"E18.2.29.0"),sQuery(id+"F13.wireOp",EDGE,"E18.3.29.0"),sQuery(id+"F13.wireOp",EDGE,"E18.6.29.0"),sQuery(id+"F13.wireOp",EDGE,"E18.9.29.0")])],"isStart":false});
            var sketch = newSketch(context, id + "F20", { "sketchPlane" : qUnion([Q0])});
            skLineSegment(sketch, "E30.bottom", {"start": v(38.55, 15.47) * mm, "end": v(41.55, 15.47) * mm});
            skLineSegment(sketch, "E30.top", {"start": v(38.55, 5.47) * mm, "end": v(41.55, 5.47) * mm});
            skLineSegment(sketch, "E30.left", {"start": v(38.55, 15.47) * mm, "end": v(38.55, 5.47) * mm});
            skLineSegment(sketch, "E30.right", {"start": v(41.55, 15.47) * mm, "end": v(41.55, 5.47) * mm});
            skSolve(sketch);
        }
        {
            var Q0;
            Q0 = qSketchRegion(id + "F20", true);
            extrude(context, id + "F21", {"entities" : qUnion([Q0]), "operationType" : NewBodyOperationType.REMOVE, "oppositeDirection" : true, "depth" : 25 * mm, "offsetDistance" : 25 * mm});
        }
    });
